# Revit family: 50717_Profilux_Led 320_SB
name_source: partatom
category: Körper
revit_build: Autodesk Revit 2015 (Build: 20140606_1530(x64)
units: mm (PartAtom-declared; Revit-internal decimal feet)

## types (1)
- ProfiLux LED 320/DMX/02
    Beam angle = 16°  + -2°
    Beschreibung = LED Technology / RGB-LED light
    Cable length = 1 m
    DMX-Channel 1 = red
    DMX-Channel 2 = green
    DMX-Channel 3 = blue
    Dim frequency = 500 Hz
    Dimensions Dxh = 125x87 mm
    Energie efficiency category = A
    Hersteller = OASE GmbH Post Box 2069, 48469 Hörstel , Germany +49 5454 80-0
    Homepage = http://www.oase-livingwater.com
    Luminous flux all on = 573 lm
    Luminous flux blue = 94 lm
    Luminous flux green = 307 lm
    Luminous flux red = 172 lm
    Material = Stainless steel 1.4404 (AISI 316L)
    Modell = ProfiLux LED 320/DMX/02
    Power connection type = Hybrid plug
    Protection class = 68 IP
    Rated current = 0.7 A
    Rated voltage = 24 V/DC
    Weight = 1.2
    Weighted energy consumption = 17.6 kWh/1000h
    oder no. = 50717
    power consumption = 16 W

## geometry (parser evidence)
native form markers: Blend x6
no freeform markers — native parametric forms only
